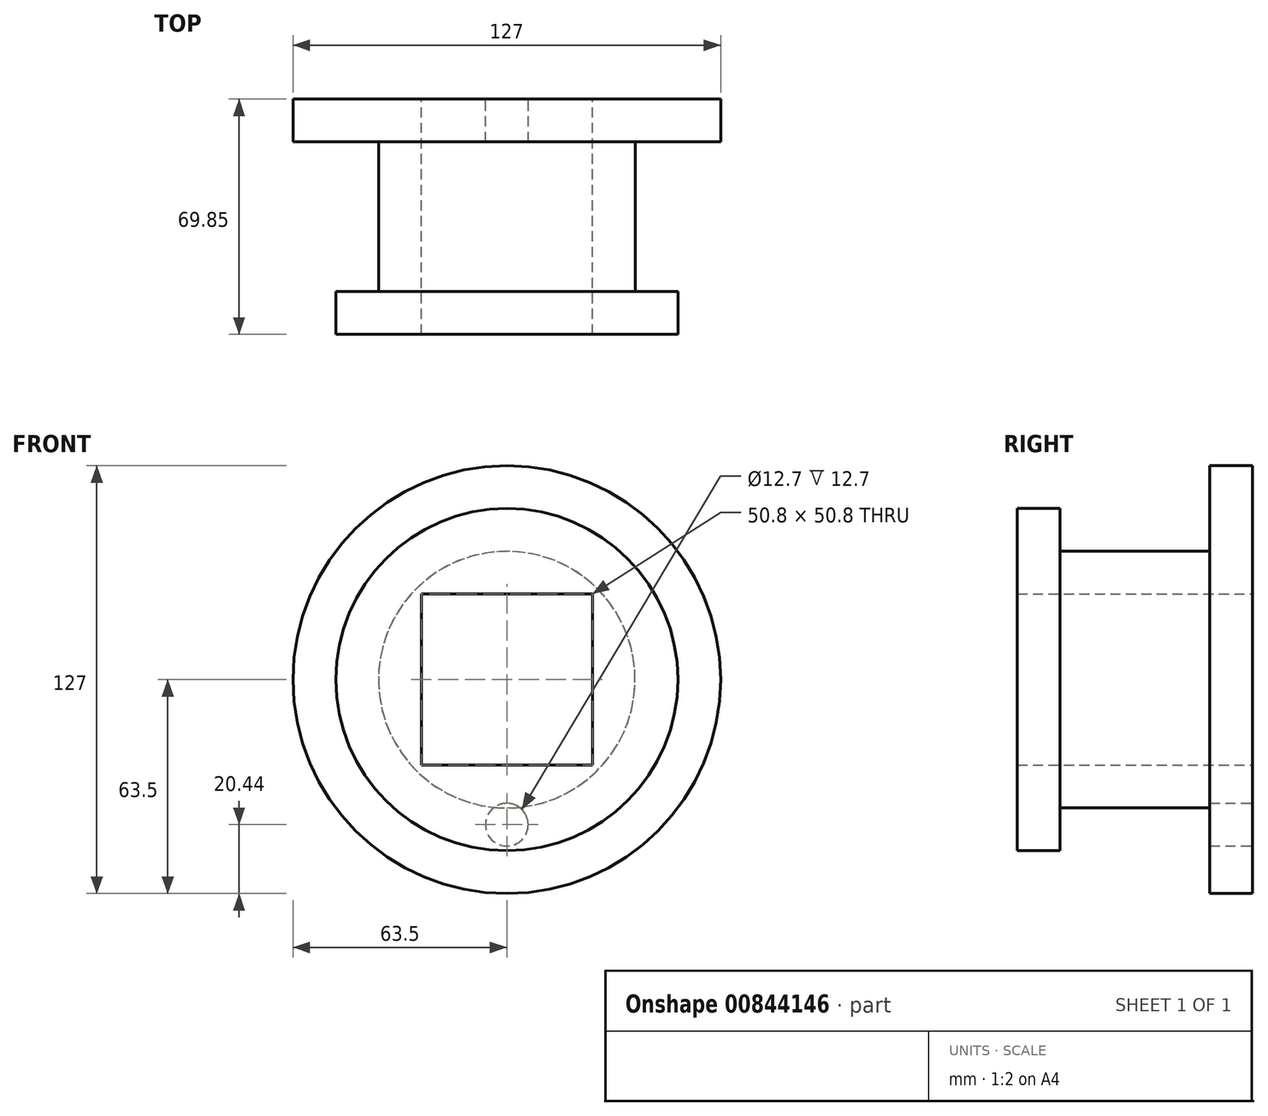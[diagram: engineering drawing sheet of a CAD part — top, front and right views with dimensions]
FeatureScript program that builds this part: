
annotation { "Feature Type Name" : "Feature", "Feature Type Description" : "" }
export const myFeature = defineFeature(function(context is Context, id is Id, definition is map)
    precondition{}
    {
        {
            var Q0;
            Q0=qCreatedBy(makeId("Front.planeOp"),FACE);
            var sketch = newSketch(context, id + "F0", { "sketchPlane" : qUnion([Q0])});
            skCircle(sketch, "E0", {"center": v(0, 0) * mm, "radius": 63.5 * mm});
            skLineSegment(sketch, "E1.bottom", {"start": v(25.4, 25.4) * mm, "end": v(-25.4, 25.4) * mm});
            skLineSegment(sketch, "E1.top", {"start": v(25.4, -25.4) * mm, "end": v(-25.4, -25.4) * mm});
            skLineSegment(sketch, "E1.left", {"start": v(25.4, 25.4) * mm, "end": v(25.4, -25.4) * mm});
            skLineSegment(sketch, "E1.right", {"start": v(-25.4, 25.4) * mm, "end": v(-25.4, -25.4) * mm});
            skSolve(sketch);
        }
        {
            var Q0;
            Q0 = qSketchRegion(id + "F0", true);
            extrude(context, id + "F1", {"entities" : qUnion([Q0]), "depth" : 12.7 * mm, "offsetDistance" : 25.4 * mm});
        }
        {
            var Q0;
            Q0=qCreatedBy(makeId("Front.planeOp"),FACE);
            var sketch = newSketch(context, id + "F2", { "sketchPlane" : qUnion([Q0])});
            skCircle(sketch, "E2", {"center": v(0, 0) * mm, "radius": 38.1 * mm});
            skSolve(sketch);
        }
        {
            var Q0;
            Q0 = qSketchRegion(id + "F2", true);
            extrude(context, id + "F3", {"entities" : qUnion([Q0]), "operationType" : NewBodyOperationType.ADD, "depth" : 57.15 * mm, "offsetDistance" : 25.4 * mm});
        }
        {
            var Q0;
            Q0=makeQuery(id+"F3.opExtrude","CAP_FACE",FACE,{"disambiguationData":[OSD([sQuery(id+"F2.wireOp",EDGE,"E2")])],"isStart":false});
            var sketch = newSketch(context, id + "F4", { "sketchPlane" : qUnion([Q0])});
            skCircle(sketch, "E3", {"center": v(0, 0) * mm, "radius": 50.8 * mm});
            skSolve(sketch);
        }
        {
            var Q0;
            Q0 = qSketchRegion(id + "F4", true);
            extrude(context, id + "F5", {"entities" : qUnion([Q0]), "operationType" : NewBodyOperationType.ADD, "depth" : 12.7 * mm, "offsetDistance" : 25.4 * mm});
        }
        {
            var Q0;
            Q0=makeQuery(id+"F3.boolean.opBoolean","MERGE",FACE,{"derivedFrom":[makeQuery(id+"F1.opExtrude","CAP_FACE",FACE,{"disambiguationData":[OSD([sQuery(id+"F0.wireOp",EDGE,"E0"),sQuery(id+"F0.wireOp",EDGE,"E1.bottom"),sQuery(id+"F0.wireOp",EDGE,"E1.top"),sQuery(id+"F0.wireOp",EDGE,"E1.left"),sQuery(id+"F0.wireOp",EDGE,"E1.right")])],"isStart":true}),makeQuery(id+"F3.opExtrude","CAP_FACE",FACE,{"disambiguationData":[OSD([sQuery(id+"F2.wireOp",EDGE,"E2")])],"isStart":true})]});
            var sketch = newSketch(context, id + "F6", { "sketchPlane" : qUnion([Q0])});
            skLineSegment(sketch, "E4.bottom", {"start": v(-25.4, 25.4) * mm, "end": v(25.4, 25.4) * mm});
            skLineSegment(sketch, "E4.top", {"start": v(-25.4, -25.4) * mm, "end": v(25.4, -25.4) * mm});
            skLineSegment(sketch, "E4.left", {"start": v(-25.4, 25.4) * mm, "end": v(-25.4, -25.4) * mm});
            skLineSegment(sketch, "E4.right", {"start": v(25.4, 25.4) * mm, "end": v(25.4, -25.4) * mm});
            skPoint(sketch, "E4.middle", {"position": v(0, 0) * mm});
            skSolve(sketch);
        }
        {
            var Q0;
            Q0 = qSketchRegion(id + "F6", true);
            extrude(context, id + "F7", {"entities" : qUnion([Q0]), "operationType" : NewBodyOperationType.REMOVE, "oppositeDirection" : true, "depth" : 82.55 * mm, "offsetDistance" : 25.4 * mm});
        }
        {
            var Q0;
            Q0=makeQuery(id+"F3.boolean.opBoolean","MERGE",FACE,{"derivedFrom":[makeQuery(id+"F1.opExtrude","CAP_FACE",FACE,{"disambiguationData":[OSD([sQuery(id+"F0.wireOp",EDGE,"E0"),sQuery(id+"F0.wireOp",EDGE,"E1.bottom"),sQuery(id+"F0.wireOp",EDGE,"E1.top"),sQuery(id+"F0.wireOp",EDGE,"E1.left"),sQuery(id+"F0.wireOp",EDGE,"E1.right")])],"isStart":true}),makeQuery(id+"F3.opExtrude","CAP_FACE",FACE,{"disambiguationData":[OSD([sQuery(id+"F2.wireOp",EDGE,"E2")])],"isStart":true})]});
            var sketch = newSketch(context, id + "F8", { "sketchPlane" : qUnion([Q0])});
            skCircle(sketch, "E5", {"center": v(0, -43.06) * mm, "radius": 6.35 * mm});
            skSolve(sketch);
        }
        {
            var Q0;
            Q0=makeQuery(id+"F8.imprint","IMPRINT",FACE,{"disambiguationData":[TD([[makeQuery(id+"F8.imprint","IMPRINT",EDGE,{"derivedFrom":sQuery(id+"F8.wireOp",EDGE,"E5")}),1.0]])]});
            extrude(context, id + "F9", {"entities" : qUnion([Q0]), "operationType" : NewBodyOperationType.REMOVE, "oppositeDirection" : true, "depth" : 12.7 * mm, "offsetDistance" : 25.4 * mm});
        }
    });
